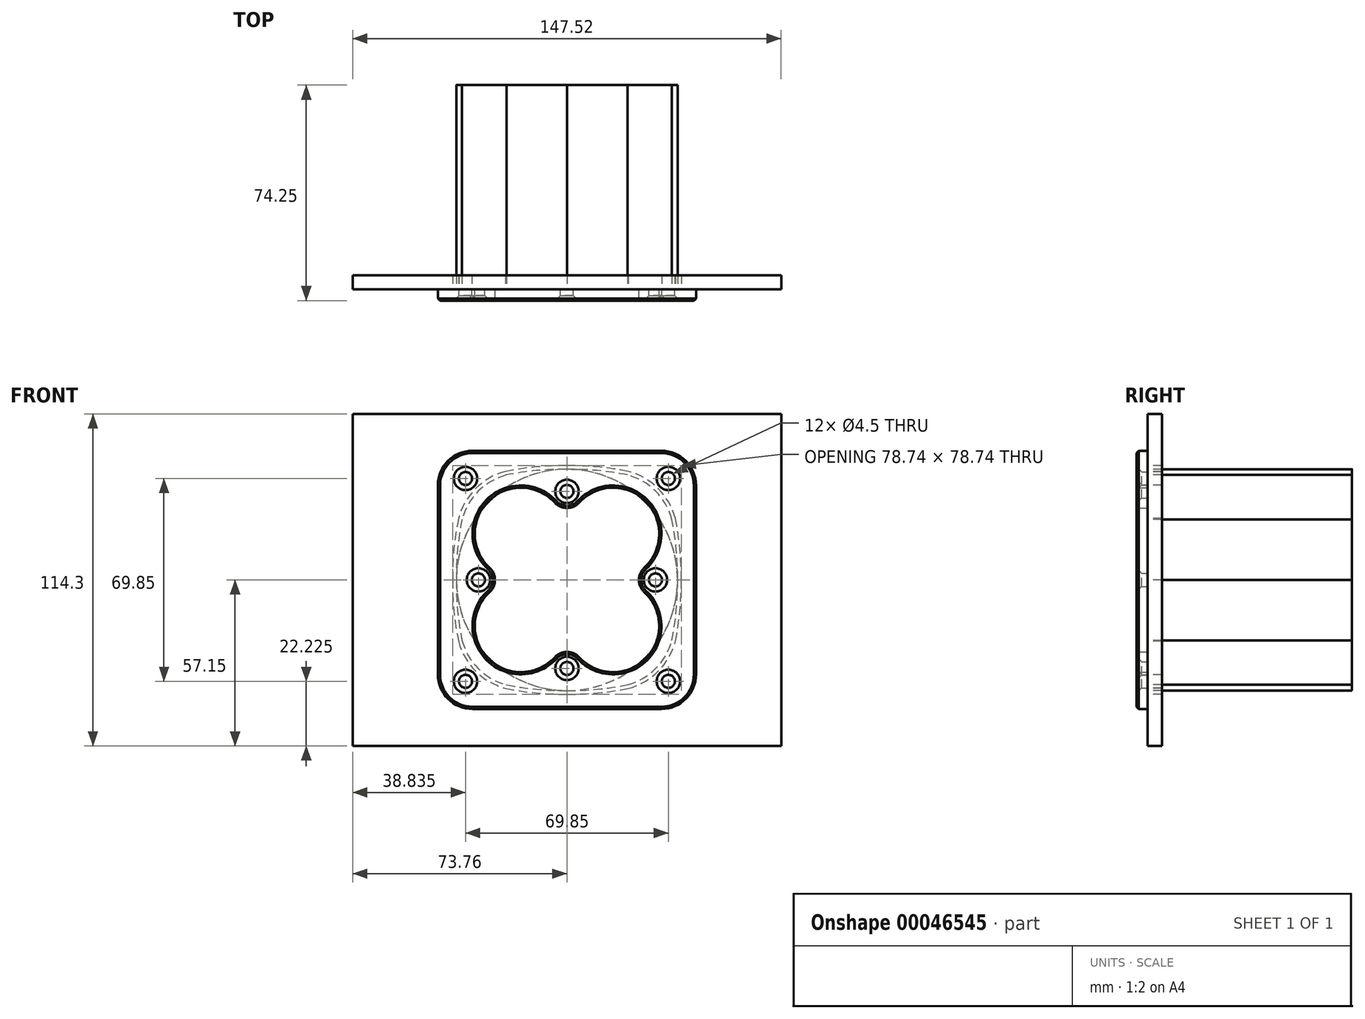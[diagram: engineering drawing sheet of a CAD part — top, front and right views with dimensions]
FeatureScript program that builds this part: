
annotation { "Feature Type Name" : "Feature", "Feature Type Description" : "" }
export const myFeature = defineFeature(function(context is Context, id is Id, definition is map)
    precondition{}
    {
        {
            var Q0;
            Q0=qCreatedBy(makeId("Front.planeOp"),FACE);
            var sketch = newSketch(context, id + "F0", { "sketchPlane" : qUnion([Q0])});
            skCircle(sketch, "E0", {"center": v(0, 0) * mm, "radius": 38.1 * mm});
            skCircle(sketch, "E1", {"center": v(0, 0) * mm, "radius": 21.59 * mm, "construction": true});
            skLineSegment(sketch, "E2", {"start": v(0, 0) * mm, "end": v(15.27, 15.27) * mm, "construction": true});
            skLineSegment(sketch, "E3", {"start": v(0, 0) * mm, "end": v(-15.27, 15.27) * mm, "construction": true});
            skLineSegment(sketch, "E4", {"start": v(0, 0) * mm, "end": v(-15.27, -15.27) * mm, "construction": true});
            skLineSegment(sketch, "E5", {"start": v(0, 0) * mm, "end": v(15.27, -15.27) * mm, "construction": true});
            skLineSegment(sketch, "E6.rect.bottom", {"start": v(34.92, -34.92) * mm, "end": v(-34.93, -34.93) * mm, "construction": true});
            skLineSegment(sketch, "E6.rect.top", {"start": v(34.92, 34.93) * mm, "end": v(-34.92, 34.92) * mm, "construction": true});
            skLineSegment(sketch, "E6.rect.left", {"start": v(34.92, -34.92) * mm, "end": v(34.92, 34.93) * mm, "construction": true});
            skLineSegment(sketch, "E6.rect.right", {"start": v(-34.93, -34.93) * mm, "end": v(-34.93, 34.92) * mm, "construction": true});
            skCircle(sketch, "E7", {"center": v(-34.92, 34.92) * mm, "radius": 2.25 * mm});
            skCircle(sketch, "E8", {"center": v(34.92, 34.93) * mm, "radius": 2.25 * mm});
            skCircle(sketch, "E9", {"center": v(34.92, -34.92) * mm, "radius": 2.25 * mm});
            skCircle(sketch, "E10", {"center": v(-34.93, -34.93) * mm, "radius": 2.25 * mm});
            skArc(sketch, "E11", {"start": v(-36.12, 20.85) * mm, "mid": v(-30.53, 30.53) * mm, "end": v(-20.85, 36.12) * mm, "construction": true});
            skArc(sketch, "E12", {"start": v(20.85, 36.12) * mm, "mid": v(30.53, 30.53) * mm, "end": v(36.12, 20.85) * mm, "construction": true});
            skArc(sketch, "E13", {"start": v(-20.85, 36.12) * mm, "mid": v(-10.48, 37.65) * mm, "end": v(0, 38.1) * mm, "construction": true});
            skArc(sketch, "E14", {"start": v(-36.12, -20.85) * mm, "mid": v(-30.53, -30.53) * mm, "end": v(-20.85, -36.12) * mm, "construction": true});
            skArc(sketch, "E15", {"start": v(36.12, -20.85) * mm, "mid": v(30.53, -30.53) * mm, "end": v(20.85, -36.12) * mm, "construction": true});
            skLineSegment(sketch, "E16", {"start": v(0, 0) * mm, "end": v(-20.85, 36.12) * mm, "construction": true});
            skLineSegment(sketch, "E17", {"start": v(0, 0) * mm, "end": v(20.85, 36.12) * mm, "construction": true});
            skArc(sketch, "E18", {"start": v(20.85, 36.12) * mm, "mid": v(10.48, 37.65) * mm, "end": v(0, 38.1) * mm, "construction": true});
            skLineSegment(sketch, "E19", {"start": v(0, 0) * mm, "end": v(-36.12, 20.85) * mm, "construction": true});
            skLineSegment(sketch, "E20", {"start": v(0, 0) * mm, "end": v(-36.12, -20.85) * mm, "construction": true});
            skLineSegment(sketch, "E21", {"start": v(0, 0) * mm, "end": v(36.12, 20.85) * mm, "construction": true});
            skLineSegment(sketch, "E22", {"start": v(0, 0) * mm, "end": v(36.12, -20.85) * mm, "construction": true});
            skLineSegment(sketch, "E23", {"start": v(0, 0) * mm, "end": v(-20.85, -36.12) * mm, "construction": true});
            skLineSegment(sketch, "E24", {"start": v(0, 0) * mm, "end": v(20.85, -36.12) * mm, "construction": true});
            skArc(sketch, "E25", {"start": v(-36.12, 20.85) * mm, "mid": v(-37.65, 10.48) * mm, "end": v(-38.1, 0) * mm, "construction": true});
            skArc(sketch, "E26", {"start": v(-38.1, 0) * mm, "mid": v(-37.65, -10.48) * mm, "end": v(-36.12, -20.85) * mm, "construction": true});
            skArc(sketch, "E27", {"start": v(-20.85, -36.12) * mm, "mid": v(-10.48, -37.65) * mm, "end": v(0, -38.1) * mm, "construction": true});
            skArc(sketch, "E28", {"start": v(0, -38.1) * mm, "mid": v(10.48, -37.65) * mm, "end": v(20.85, -36.12) * mm, "construction": true});
            skArc(sketch, "E29", {"start": v(38.1, 0) * mm, "mid": v(37.65, 10.48) * mm, "end": v(36.12, 20.85) * mm, "construction": true});
            skArc(sketch, "E30", {"start": v(36.12, -20.85) * mm, "mid": v(37.65, -10.48) * mm, "end": v(38.1, 0) * mm, "construction": true});
            skArc(sketch, "E31.0", {"start": v(-37.36, 21.14) * mm, "mid": v(-31.43, 31.43) * mm, "end": v(-21.14, 37.36) * mm});
            skArc(sketch, "E31.1", {"start": v(37.36, -21.14) * mm, "mid": v(38.91, -10.62) * mm, "end": v(39.37, 0) * mm});
            skArc(sketch, "E31.2", {"start": v(39.37, 0) * mm, "mid": v(38.91, 10.62) * mm, "end": v(37.36, 21.14) * mm});
            skArc(sketch, "E31.3", {"start": v(21.14, 37.36) * mm, "mid": v(31.43, 31.43) * mm, "end": v(37.36, 21.14) * mm});
            skArc(sketch, "E31.4", {"start": v(21.14, 37.36) * mm, "mid": v(10.62, 38.91) * mm, "end": v(0, 39.37) * mm});
            skArc(sketch, "E31.5", {"start": v(37.36, -21.14) * mm, "mid": v(31.43, -31.43) * mm, "end": v(21.14, -37.36) * mm});
            skArc(sketch, "E31.6", {"start": v(-21.14, 37.36) * mm, "mid": v(-10.62, 38.91) * mm, "end": v(0, 39.37) * mm});
            skArc(sketch, "E31.7", {"start": v(0, -39.37) * mm, "mid": v(10.62, -38.91) * mm, "end": v(21.14, -37.36) * mm});
            skArc(sketch, "E31.8", {"start": v(-21.14, -37.36) * mm, "mid": v(-10.62, -38.91) * mm, "end": v(0, -39.37) * mm});
            skArc(sketch, "E31.9", {"start": v(-37.36, -21.14) * mm, "mid": v(-31.43, -31.43) * mm, "end": v(-21.14, -37.36) * mm});
            skArc(sketch, "E31.10", {"start": v(-39.37, 0) * mm, "mid": v(-38.91, -10.62) * mm, "end": v(-37.36, -21.14) * mm});
            skArc(sketch, "E31.11", {"start": v(-37.36, 21.14) * mm, "mid": v(-38.91, 10.62) * mm, "end": v(-39.37, 0) * mm});
            skLineSegment(sketch, "E32.rect.bottom", {"start": v(73.76, -57.15) * mm, "end": v(-73.76, -57.15) * mm});
            skLineSegment(sketch, "E32.rect.top", {"start": v(73.76, 57.15) * mm, "end": v(-73.76, 57.15) * mm});
            skLineSegment(sketch, "E32.rect.left", {"start": v(73.76, -57.15) * mm, "end": v(73.76, 57.15) * mm});
            skLineSegment(sketch, "E32.rect.right", {"start": v(-73.76, -57.15) * mm, "end": v(-73.76, 57.15) * mm});
            skSolve(sketch);
        }
        {
            var Q0;
            Q0=makeQuery(id+"F0.imprint","IMPRINT",FACE,{"disambiguationData":[TD([[makeQuery(id+"F0.imprint","IMPRINT",EDGE,{"derivedFrom":sQuery(id+"F0.wireOp",EDGE,"E7")}),-1.0]])]});
            var Q1;
            Q1=makeQuery(id+"F0.imprint","IMPRINT",FACE,{"disambiguationData":[TD([[makeQuery(id+"F0.imprint","IMPRINT",EDGE,{"derivedFrom":sQuery(id+"F0.wireOp",EDGE,"E0")}),1.0]])]});
            var Q2;
            Q2=sQuery(id+"F0.wireOp",EDGE,"E7");
            var Q3;
            Q3=sQuery(id+"F0.wireOp",EDGE,"af173d0e-fcfb-48a2-ad59-56037ec1813f.6");
            var Q4;
            Q4=sQuery(id+"F0.wireOp",EDGE,"af173d0e-fcfb-48a2-ad59-56037ec1813f.0");
            var Q5;
            Q5=sQuery(id+"F0.wireOp",EDGE,"af173d0e-fcfb-48a2-ad59-56037ec1813f.11");
            var Q6;
            Q6=sQuery(id+"F0.wireOp",EDGE,"af173d0e-fcfb-48a2-ad59-56037ec1813f.10");
            var Q7;
            Q7=sQuery(id+"F0.wireOp",EDGE,"af173d0e-fcfb-48a2-ad59-56037ec1813f.9");
            var Q8;
            Q8=sQuery(id+"F0.wireOp",EDGE,"af173d0e-fcfb-48a2-ad59-56037ec1813f.8");
            var Q9;
            Q9=sQuery(id+"F0.wireOp",EDGE,"E0");
            var Q10;
            Q10=sQuery(id+"F0.wireOp",EDGE,"af173d0e-fcfb-48a2-ad59-56037ec1813f.7");
            var Q11;
            Q11=sQuery(id+"F0.wireOp",EDGE,"af173d0e-fcfb-48a2-ad59-56037ec1813f.5");
            var Q12;
            Q12=sQuery(id+"F0.wireOp",EDGE,"af173d0e-fcfb-48a2-ad59-56037ec1813f.1");
            var Q13;
            Q13=sQuery(id+"F0.wireOp",EDGE,"af173d0e-fcfb-48a2-ad59-56037ec1813f.2");
            var Q14;
            Q14=sQuery(id+"F0.wireOp",EDGE,"af173d0e-fcfb-48a2-ad59-56037ec1813f.3");
            var Q15;
            Q15=sQuery(id+"F0.wireOp",EDGE,"af173d0e-fcfb-48a2-ad59-56037ec1813f.4");
            var Q16;
            Q16=sQuery(id+"F0.wireOp",EDGE,"E10");
            var Q17;
            Q17=sQuery(id+"F0.wireOp",EDGE,"E8");
            var Q18;
            Q18=sQuery(id+"F0.wireOp",EDGE,"E9");
            extrude(context, id + "F1", {"entities" : qUnion([Q0, Q1]), "surfaceEntities" : qUnion([Q2, Q3, Q4, Q5, Q6, Q7, Q8, Q9, Q10, Q11, Q12, Q13, Q14, Q15, Q16, Q17, Q18]), "oppositeDirection" : true, "depth" : 4.9 * mm});
        }
        {
            var Q0;
            Q0=qCreatedBy(makeId("Front.planeOp"),FACE);
            var sketch = newSketch(context, id + "F2", { "sketchPlane" : qUnion([Q0])});
            skLineSegment(sketch, "E33.rect.bottom", {"start": v(32.51, -44.45) * mm, "end": v(-32.51, -44.45) * mm});
            skLineSegment(sketch, "E33.rect.top", {"start": v(32.51, 44.45) * mm, "end": v(-32.51, 44.45) * mm});
            skLineSegment(sketch, "E33.rect.left", {"start": v(44.45, -32.51) * mm, "end": v(44.45, 32.51) * mm});
            skLineSegment(sketch, "E33.rect.right", {"start": v(-44.45, -32.51) * mm, "end": v(-44.45, 32.51) * mm});
            skPoint(sketch, "E33.rect.middle", {"position": v(0, 0) * mm});
            skPoint(sketch, "E34.visualSharp", {"position": v(-44.45, 44.45) * mm});
            skArc(sketch, "E34.filletArc", {"start": v(-32.51, 44.45) * mm, "mid": v(-40.95, 40.95) * mm, "end": v(-44.45, 32.51) * mm});
            skPoint(sketch, "E35.visualSharp", {"position": v(44.45, 44.45) * mm});
            skArc(sketch, "E35.filletArc", {"start": v(44.45, 32.51) * mm, "mid": v(40.95, 40.95) * mm, "end": v(32.51, 44.45) * mm});
            skPoint(sketch, "E36.visualSharp", {"position": v(44.45, -44.45) * mm});
            skArc(sketch, "E36.filletArc", {"start": v(32.51, -44.45) * mm, "mid": v(40.95, -40.95) * mm, "end": v(44.45, -32.51) * mm});
            skPoint(sketch, "E37.visualSharp", {"position": v(-44.45, -44.45) * mm});
            skArc(sketch, "E37.filletArc", {"start": v(-44.45, -32.51) * mm, "mid": v(-40.95, -40.95) * mm, "end": v(-32.51, -44.45) * mm});
            skCircle(sketch, "E38.0", {"center": v(-34.92, 34.92) * mm, "radius": 2.25 * mm});
            skCircle(sketch, "E39.0", {"center": v(34.92, 34.93) * mm, "radius": 2.25 * mm});
            skCircle(sketch, "E40.0", {"center": v(34.92, -34.92) * mm, "radius": 2.25 * mm});
            skCircle(sketch, "E41.0", {"center": v(-34.93, -34.93) * mm, "radius": 2.25 * mm});
            skArc(sketch, "E42", {"start": v(-4.2, 26.62) * mm, "mid": v(-27.1, 27.1) * mm, "end": v(-26.62, 4.2) * mm});
            skArc(sketch, "E43", {"start": v(26.62, 4.2) * mm, "mid": v(27.1, 27.1) * mm, "end": v(4.2, 26.62) * mm});
            skArc(sketch, "E44", {"start": v(-26.62, -4.2) * mm, "mid": v(-27.1, -27.1) * mm, "end": v(-4.2, -26.62) * mm});
            skArc(sketch, "E45", {"start": v(4.2, -26.62) * mm, "mid": v(27.1, -27.1) * mm, "end": v(26.62, -4.2) * mm});
            skCircle(sketch, "E46", {"center": v(0, 30.48) * mm, "radius": 2.25 * mm});
            skCircle(sketch, "E47", {"center": v(-30.48, 0) * mm, "radius": 2.25 * mm});
            skCircle(sketch, "E48", {"center": v(0, -30.48) * mm, "radius": 2.25 * mm});
            skCircle(sketch, "E49", {"center": v(30.48, 0) * mm, "radius": 2.25 * mm});
            skLineSegment(sketch, "E50.rect.bottom", {"start": v(30.48, -30.48) * mm, "end": v(-30.48, -30.48) * mm, "construction": true});
            skLineSegment(sketch, "E50.rect.top", {"start": v(30.48, 30.48) * mm, "end": v(-30.48, 30.48) * mm, "construction": true});
            skLineSegment(sketch, "E50.rect.left", {"start": v(30.48, -30.48) * mm, "end": v(30.48, 30.48) * mm, "construction": true});
            skLineSegment(sketch, "E50.rect.right", {"start": v(-30.48, -30.48) * mm, "end": v(-30.48, 30.48) * mm, "construction": true});
            skArc(sketch, "E51", {"start": v(-4.2, 26.62) * mm, "mid": v(0, 24.78) * mm, "end": v(4.2, 26.62) * mm});
            skArc(sketch, "E52", {"start": v(-26.62, -4.2) * mm, "mid": v(-24.78, 0) * mm, "end": v(-26.62, 4.2) * mm});
            skArc(sketch, "E53", {"start": v(4.2, -26.62) * mm, "mid": v(0, -24.78) * mm, "end": v(-4.2, -26.62) * mm});
            skArc(sketch, "E54", {"start": v(26.62, 4.2) * mm, "mid": v(24.78, 0) * mm, "end": v(26.62, -4.2) * mm});
            skSolve(sketch);
        }
        {
            var Q0;
            Q0 = qSketchRegion(id + "F2", true);
            extrude(context, id + "F3", {"entities" : qUnion([Q0]), "depth" : 3.9 * mm});
        }
        {
            var Q0;
            Q0=makeQuery(id+"F3.opExtrude","CAP_EDGE",EDGE,{"disambiguationData":[OSD([sQuery(id+"F2.wireOp",EDGE,"E42")])],"isStart":false});
            var Q1;
            Q1=makeQuery(id+"F3.opExtrude","CAP_EDGE",EDGE,{"disambiguationData":[OSD([sQuery(id+"F2.wireOp",EDGE,"E33.rect.left")])],"isStart":false});
            chamfer(context, id + "F4", {"entities" : qUnion([Q0, Q1]), "width" : 0.76 * mm, "tangentPropagation" : true});
        }
        {
            var Q0;
            Q0=makeQuery(id+"F3.opExtrude","CAP_EDGE",EDGE,{"disambiguationData":[OSD([sQuery(id+"F2.wireOp",EDGE,"E46")])],"isStart":false});
            var Q1;
            Q1=makeQuery(id+"F3.opExtrude","CAP_EDGE",EDGE,{"disambiguationData":[OSD([sQuery(id+"F2.wireOp",EDGE,"E38.0")])],"isStart":false});
            var Q2;
            Q2=makeQuery(id+"F3.opExtrude","CAP_EDGE",EDGE,{"disambiguationData":[OSD([sQuery(id+"F2.wireOp",EDGE,"E47")])],"isStart":false});
            var Q3;
            Q3=makeQuery(id+"F3.opExtrude","CAP_EDGE",EDGE,{"disambiguationData":[OSD([sQuery(id+"F2.wireOp",EDGE,"E41.0")])],"isStart":false});
            var Q4;
            Q4=makeQuery(id+"F3.opExtrude","CAP_EDGE",EDGE,{"disambiguationData":[OSD([sQuery(id+"F2.wireOp",EDGE,"E48")])],"isStart":false});
            var Q5;
            Q5=makeQuery(id+"F3.opExtrude","CAP_EDGE",EDGE,{"disambiguationData":[OSD([sQuery(id+"F2.wireOp",EDGE,"E40.0")])],"isStart":false});
            var Q6;
            Q6=makeQuery(id+"F3.opExtrude","CAP_EDGE",EDGE,{"disambiguationData":[OSD([sQuery(id+"F2.wireOp",EDGE,"E49")])],"isStart":false});
            var Q7;
            Q7=makeQuery(id+"F3.opExtrude","CAP_EDGE",EDGE,{"disambiguationData":[OSD([sQuery(id+"F2.wireOp",EDGE,"E39.0")])],"isStart":false});
            chamfer(context, id + "F5", {"entities" : qUnion([Q0, Q1, Q2, Q3, Q4, Q5, Q6, Q7]), "width" : 1.78 * mm, "tangentPropagation" : true});
        }
        {
            var Q0;
            Q0=qCreatedBy(makeId("Front.planeOp"),FACE);
            var sketch = newSketch(context, id + "F6", { "sketchPlane" : qUnion([Q0])});
            skArc(sketch, "E55.0", {"start": v(-36.12, 20.85) * mm, "mid": v(-30.53, 30.53) * mm, "end": v(-20.85, 36.12) * mm});
            skArc(sketch, "E55.1", {"start": v(-20.85, 36.12) * mm, "mid": v(-10.48, 37.65) * mm, "end": v(0, 38.1) * mm});
            skArc(sketch, "E55.2", {"start": v(20.85, 36.12) * mm, "mid": v(10.48, 37.65) * mm, "end": v(0, 38.1) * mm});
            skArc(sketch, "E55.3", {"start": v(20.85, 36.12) * mm, "mid": v(30.53, 30.53) * mm, "end": v(36.12, 20.85) * mm});
            skArc(sketch, "E55.4", {"start": v(38.1, 0) * mm, "mid": v(37.65, 10.48) * mm, "end": v(36.12, 20.85) * mm});
            skArc(sketch, "E55.5", {"start": v(36.12, -20.85) * mm, "mid": v(37.65, -10.48) * mm, "end": v(38.1, 0) * mm});
            skArc(sketch, "E55.6", {"start": v(36.12, -20.85) * mm, "mid": v(30.53, -30.53) * mm, "end": v(20.85, -36.12) * mm});
            skArc(sketch, "E55.7", {"start": v(0, -38.1) * mm, "mid": v(10.48, -37.65) * mm, "end": v(20.85, -36.12) * mm});
            skArc(sketch, "E55.8", {"start": v(-20.85, -36.12) * mm, "mid": v(-10.48, -37.65) * mm, "end": v(0, -38.1) * mm});
            skArc(sketch, "E55.9", {"start": v(-36.12, -20.85) * mm, "mid": v(-30.53, -30.53) * mm, "end": v(-20.85, -36.12) * mm});
            skArc(sketch, "E55.10", {"start": v(-38.1, 0) * mm, "mid": v(-37.65, -10.48) * mm, "end": v(-36.12, -20.85) * mm});
            skArc(sketch, "E55.11", {"start": v(-36.12, 20.85) * mm, "mid": v(-37.65, 10.48) * mm, "end": v(-38.1, 0) * mm});
            skSolve(sketch);
        }
        {
            var Q0;
            Q0 = qSketchRegion(id + "F6", true);
            extrude(context, id + "F7", {"entities" : qUnion([Q0]), "oppositeDirection" : true, "depth" : 70.36 * mm});
        }
    });
